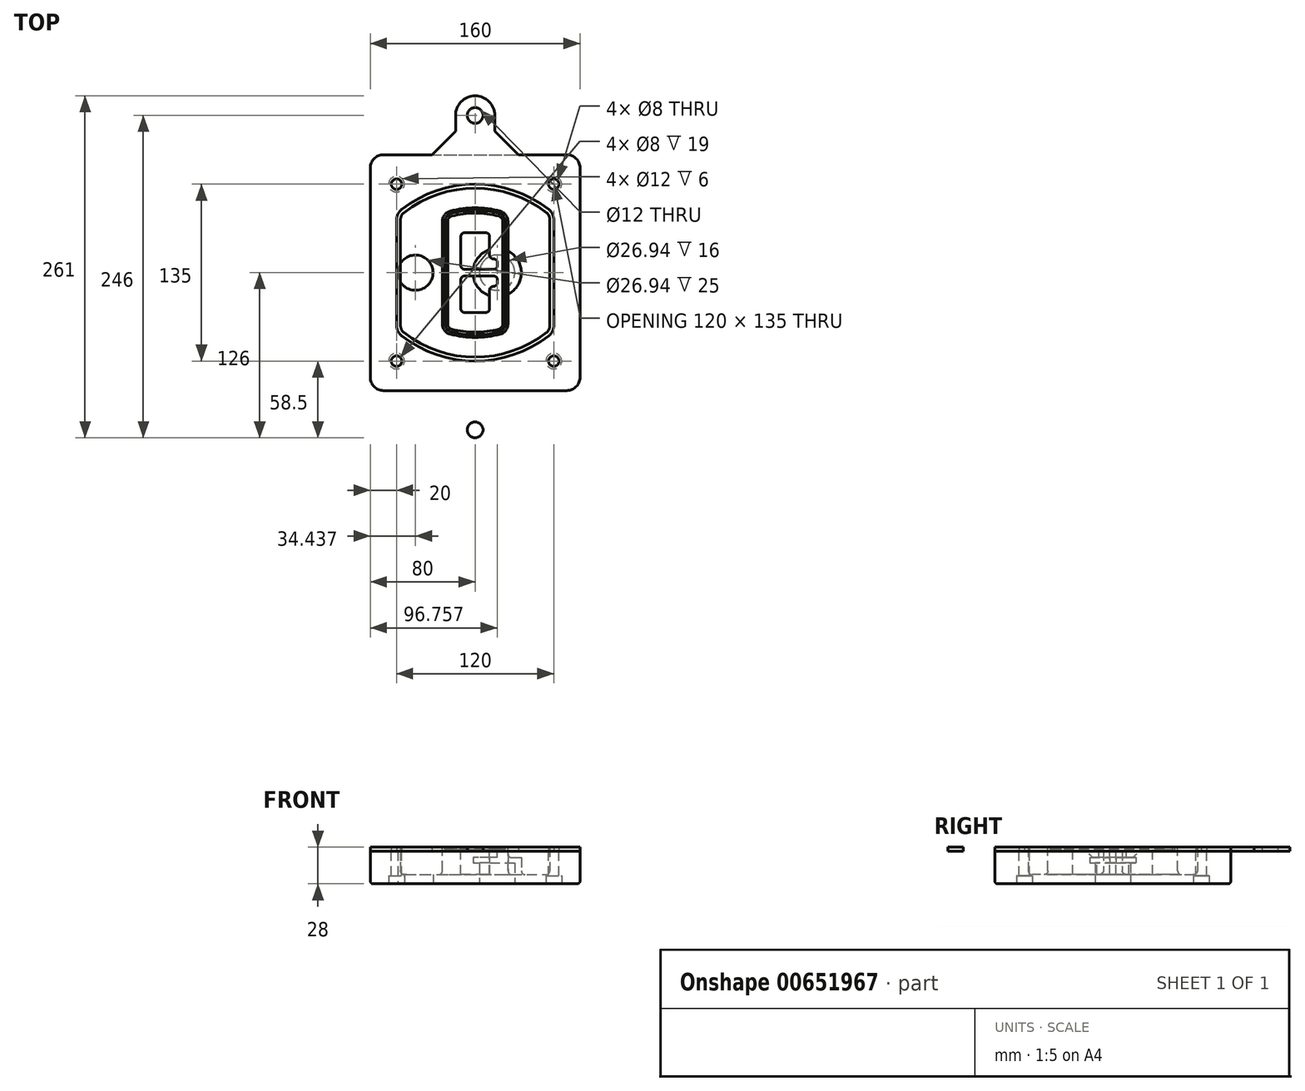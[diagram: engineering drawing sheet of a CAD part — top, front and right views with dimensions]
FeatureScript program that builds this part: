
annotation { "Feature Type Name" : "Feature", "Feature Type Description" : "" }
export const myFeature = defineFeature(function(context is Context, id is Id, definition is map)
    precondition{}
    {
        {
            var Q0;
            Q0=qCreatedBy(makeId("Top.planeOp"),FACE);
            var sketch = newSketch(context, id + "F0", { "sketchPlane" : qUnion([Q0])});
            skPoint(sketch, "E0.rect.middle", {"position": v(0, 0) * mm});
            skLineSegment(sketch, "E1.bottom", {"start": v(-70, -90) * mm, "end": v(70, -90) * mm});
            skLineSegment(sketch, "E1.top", {"start": v(-70, 90) * mm, "end": v(70, 90) * mm});
            skLineSegment(sketch, "E1.left", {"start": v(-80, -80) * mm, "end": v(-80, 80) * mm});
            skLineSegment(sketch, "E1.right", {"start": v(80, -80) * mm, "end": v(80, 80) * mm});
            skLineSegment(sketch, "E2", {"start": v(-80, 90) * mm, "end": v(80, -90) * mm, "construction": true});
            skLineSegment(sketch, "E3", {"start": v(80, 90) * mm, "end": v(-80, -90) * mm, "construction": true});
            skCircle(sketch, "E4", {"center": v(-60, 67.5) * mm, "radius": 4 * mm});
            skCircle(sketch, "E5", {"center": v(60, 67.5) * mm, "radius": 4 * mm});
            skCircle(sketch, "E6", {"center": v(60, -67.5) * mm, "radius": 4 * mm});
            skCircle(sketch, "E7", {"center": v(-60, -67.5) * mm, "radius": 4 * mm});
            skLineSegment(sketch, "E8", {"start": v(-60, 67.5) * mm, "end": v(60, 67.5) * mm, "construction": true});
            skLineSegment(sketch, "E9", {"start": v(60, 67.5) * mm, "end": v(60, -67.5) * mm, "construction": true});
            skLineSegment(sketch, "E10", {"start": v(60, -67.5) * mm, "end": v(-60, -67.5) * mm, "construction": true});
            skLineSegment(sketch, "E11", {"start": v(-60, -67.5) * mm, "end": v(-60, 67.5) * mm, "construction": true});
            skLineSegment(sketch, "E12", {"start": v(-60, 40.3) * mm, "end": v(-60, -40.3) * mm});
            skLineSegment(sketch, "E13", {"start": v(60, 40.3) * mm, "end": v(60, -40.3) * mm});
            skArc(sketch, "E14", {"start": v(56.15, 48.18) * mm, "mid": v(0, 67.5) * mm, "end": v(-56.15, 48.18) * mm});
            skArc(sketch, "E15", {"start": v(-56.15, -48.18) * mm, "mid": v(0, -67.5) * mm, "end": v(56.15, -48.18) * mm});
            skLineSegment(sketch, "E16", {"start": v(-60, 0) * mm, "end": v(60, 0) * mm, "construction": true});
            skPoint(sketch, "E17.visualSharp", {"position": v(-60, -45) * mm});
            skArc(sketch, "E17.filletArc", {"start": v(-60, -40.3) * mm, "mid": v(-58.99, -44.68) * mm, "end": v(-56.15, -48.18) * mm});
            skPoint(sketch, "E18.visualSharp", {"position": v(-60, 45) * mm});
            skArc(sketch, "E18.filletArc", {"start": v(-56.15, 48.18) * mm, "mid": v(-58.99, 44.68) * mm, "end": v(-60, 40.3) * mm});
            skPoint(sketch, "E19.visualSharp", {"position": v(60, 45) * mm});
            skArc(sketch, "E19.filletArc", {"start": v(60, 40.3) * mm, "mid": v(58.99, 44.68) * mm, "end": v(56.15, 48.18) * mm});
            skPoint(sketch, "E20.visualSharp", {"position": v(60, -45) * mm});
            skArc(sketch, "E20.filletArc", {"start": v(56.15, -48.18) * mm, "mid": v(58.99, -44.68) * mm, "end": v(60, -40.3) * mm});
            skPoint(sketch, "E21.visualSharp", {"position": v(-80, 90) * mm});
            skArc(sketch, "E21.filletArc", {"start": v(-70, 90) * mm, "mid": v(-77.07, 87.07) * mm, "end": v(-80, 80) * mm});
            skPoint(sketch, "E22.visualSharp", {"position": v(80, 90) * mm});
            skArc(sketch, "E22.filletArc", {"start": v(80, 80) * mm, "mid": v(77.07, 87.07) * mm, "end": v(70, 90) * mm});
            skPoint(sketch, "E23.visualSharp", {"position": v(80, -90) * mm});
            skArc(sketch, "E23.filletArc", {"start": v(70, -90) * mm, "mid": v(77.07, -87.07) * mm, "end": v(80, -80) * mm});
            skPoint(sketch, "E24.visualSharp", {"position": v(-80, -90) * mm});
            skArc(sketch, "E24.filletArc", {"start": v(-80, -80) * mm, "mid": v(-77.07, -87.07) * mm, "end": v(-70, -90) * mm});
            skArc(sketch, "E25.0", {"start": v(57, 40.3) * mm, "mid": v(56.3, 43.36) * mm, "end": v(54.3, 45.81) * mm});
            skLineSegment(sketch, "E25.1", {"start": v(57, 40.3) * mm, "end": v(57, -40.3) * mm});
            skArc(sketch, "E25.2", {"start": v(54.3, -45.81) * mm, "mid": v(56.3, -43.36) * mm, "end": v(57, -40.3) * mm});
            skArc(sketch, "E25.3", {"start": v(-54.3, -45.81) * mm, "mid": v(0, -64.5) * mm, "end": v(54.3, -45.81) * mm});
            skArc(sketch, "E25.4", {"start": v(-57, -40.3) * mm, "mid": v(-56.3, -43.36) * mm, "end": v(-54.3, -45.81) * mm});
            skArc(sketch, "E25.5", {"start": v(54.3, 45.81) * mm, "mid": v(0, 64.5) * mm, "end": v(-54.3, 45.81) * mm});
            skLineSegment(sketch, "E25.6", {"start": v(-57, 40.3) * mm, "end": v(-57, -40.3) * mm});
            skArc(sketch, "E25.7", {"start": v(-54.3, 45.81) * mm, "mid": v(-56.3, 43.36) * mm, "end": v(-57, 40.3) * mm});
            skArc(sketch, "E26.0", {"start": v(-58.62, 51.33) * mm, "mid": v(-62.58, 46.43) * mm, "end": v(-64, 40.3) * mm});
            skArc(sketch, "E26.1", {"start": v(58.62, 51.33) * mm, "mid": v(0, 71.5) * mm, "end": v(-58.62, 51.33) * mm});
            skArc(sketch, "E26.2", {"start": v(64, 40.3) * mm, "mid": v(62.58, 46.43) * mm, "end": v(58.62, 51.33) * mm});
            skLineSegment(sketch, "E26.3", {"start": v(64, 40.3) * mm, "end": v(64, -40.3) * mm});
            skArc(sketch, "E26.4", {"start": v(58.62, -51.33) * mm, "mid": v(62.58, -46.43) * mm, "end": v(64, -40.3) * mm});
            skLineSegment(sketch, "E26.5", {"start": v(-64, 40.3) * mm, "end": v(-64, -40.3) * mm});
            skArc(sketch, "E26.6", {"start": v(-58.62, -51.33) * mm, "mid": v(0, -71.5) * mm, "end": v(58.62, -51.33) * mm});
            skArc(sketch, "E26.7", {"start": v(-64, -40.3) * mm, "mid": v(-62.58, -46.43) * mm, "end": v(-58.62, -51.33) * mm});
            skSolve(sketch);
        }
        {
            var Q0;
            Q0=makeQuery(id+"F0.imprint","IMPRINT",FACE,{"disambiguationData":[TD([[makeQuery(id+"F0.imprint","IMPRINT",EDGE,{"derivedFrom":sQuery(id+"F0.wireOp",EDGE,"E1.bottom")}),1.0]])]});
            var Q1;
            Q1=makeQuery(id+"F0.imprint","IMPRINT",FACE,{"disambiguationData":[TD([[makeQuery(id+"F0.imprint","IMPRINT",EDGE,{"derivedFrom":sQuery(id+"F0.wireOp",EDGE,"E12")}),1.0]])]});
            var Q2;
            Q2=makeQuery(id+"F0.imprint","IMPRINT",FACE,{"disambiguationData":[TD([[makeQuery(id+"F0.imprint","IMPRINT",EDGE,{"derivedFrom":sQuery(id+"F0.wireOp",EDGE,"E25.0")}),1.0]])]});
            var Q3;
            Q3=makeQuery(id+"F0.imprint","IMPRINT",FACE,{"disambiguationData":[TD([[makeQuery(id+"F0.imprint","IMPRINT",EDGE,{"derivedFrom":sQuery(id+"F0.wireOp",EDGE,"E12")}),-1.0]])]});
            extrude(context, id + "F1", {"entities" : qUnion([Q0, Q1, Q2, Q3]), "oppositeDirection" : true, "depth" : 25 * mm});
        }
        {
            var Q0;
            Q0=makeQuery(id+"F0.imprint","IMPRINT",FACE,{"disambiguationData":[TD([[makeQuery(id+"F0.imprint","IMPRINT",EDGE,{"derivedFrom":sQuery(id+"F0.wireOp",EDGE,"E12")}),1.0]])]});
            extrude(context, id + "F2", {"entities" : qUnion([Q0]), "operationType" : NewBodyOperationType.ADD, "depth" : 3 * mm});
        }
        {
            var Q0;
            Q0=makeQuery(id+"F0.imprint","IMPRINT",FACE,{"disambiguationData":[TD([[makeQuery(id+"F0.imprint","IMPRINT",EDGE,{"derivedFrom":sQuery(id+"F0.wireOp",EDGE,"E25.0")}),1.0]])]});
            extrude(context, id + "F3", {"entities" : qUnion([Q0]), "operationType" : NewBodyOperationType.REMOVE, "oppositeDirection" : true, "depth" : 18 * mm});
        }
        {
            var Q0;
            Q0=makeQuery(id+"F2.opExtrude","CAP_FACE",FACE,{"disambiguationData":[OSD([sQuery(id+"F0.wireOp",EDGE,"E12"),sQuery(id+"F0.wireOp",EDGE,"E13"),sQuery(id+"F0.wireOp",EDGE,"E14"),sQuery(id+"F0.wireOp",EDGE,"E15"),sQuery(id+"F0.wireOp",EDGE,"E17.filletArc"),sQuery(id+"F0.wireOp",EDGE,"E18.filletArc"),sQuery(id+"F0.wireOp",EDGE,"E19.filletArc"),sQuery(id+"F0.wireOp",EDGE,"E20.filletArc"),sQuery(id+"F0.wireOp",EDGE,"E25.0"),sQuery(id+"F0.wireOp",EDGE,"E25.1"),sQuery(id+"F0.wireOp",EDGE,"E25.2"),sQuery(id+"F0.wireOp",EDGE,"E25.3"),sQuery(id+"F0.wireOp",EDGE,"E25.4"),sQuery(id+"F0.wireOp",EDGE,"E25.5"),sQuery(id+"F0.wireOp",EDGE,"E25.6"),sQuery(id+"F0.wireOp",EDGE,"E25.7")])],"isStart":false});
            var sketch = newSketch(context, id + "F4", { "sketchPlane" : qUnion([Q0])});
            skArc(sketch, "E27.0", {"start": v(-19.08, -46.97) * mm, "mid": v(0, -49.5) * mm, "end": v(19.08, -46.97) * mm});
            skArc(sketch, "E28.0", {"start": v(19.08, 46.97) * mm, "mid": v(0, 49.5) * mm, "end": v(-19.08, 46.97) * mm});
            skLineSegment(sketch, "E29", {"start": v(-25, 39.25) * mm, "end": v(-25, -39.25) * mm});
            skLineSegment(sketch, "E30", {"start": v(25, 39.25) * mm, "end": v(25, -39.25) * mm});
            skLineSegment(sketch, "E31", {"start": v(-25, 45.1) * mm, "end": v(25, 45.1) * mm, "construction": true});
            skLineSegment(sketch, "E32", {"start": v(-25, -45.1) * mm, "end": v(25, -45.1) * mm, "construction": true});
            skPoint(sketch, "E33.visualSharp", {"position": v(-25, 45.1) * mm});
            skArc(sketch, "E33.filletArc", {"start": v(-19.08, 46.97) * mm, "mid": v(-23.35, 44.11) * mm, "end": v(-25, 39.25) * mm});
            skPoint(sketch, "E34.visualSharp", {"position": v(25, 45.1) * mm});
            skArc(sketch, "E34.filletArc", {"start": v(25, 39.25) * mm, "mid": v(23.35, 44.11) * mm, "end": v(19.08, 46.97) * mm});
            skPoint(sketch, "E35.visualSharp", {"position": v(25, -45.1) * mm});
            skArc(sketch, "E35.filletArc", {"start": v(19.08, -46.97) * mm, "mid": v(23.35, -44.11) * mm, "end": v(25, -39.25) * mm});
            skPoint(sketch, "E36.visualSharp", {"position": v(-25, -45.1) * mm});
            skArc(sketch, "E36.filletArc", {"start": v(-25, -39.25) * mm, "mid": v(-23.35, -44.11) * mm, "end": v(-19.08, -46.97) * mm});
            skArc(sketch, "E37.0", {"start": v(54.3, 45.81) * mm, "mid": v(0, 64.5) * mm, "end": v(-54.3, 45.81) * mm});
            skArc(sketch, "E37.1", {"start": v(-54.3, 45.81) * mm, "mid": v(-56.3, 43.36) * mm, "end": v(-57, 40.3) * mm});
            skLineSegment(sketch, "E37.2", {"start": v(-57, 40.3) * mm, "end": v(-57, -40.3) * mm});
            skArc(sketch, "E37.3", {"start": v(-57, -40.3) * mm, "mid": v(-56.3, -43.36) * mm, "end": v(-54.3, -45.81) * mm});
            skArc(sketch, "E37.4", {"start": v(-54.3, -45.81) * mm, "mid": v(0, -64.5) * mm, "end": v(54.3, -45.81) * mm});
            skArc(sketch, "E37.5", {"start": v(54.3, -45.81) * mm, "mid": v(56.3, -43.36) * mm, "end": v(57, -40.3) * mm});
            skLineSegment(sketch, "E37.6", {"start": v(57, 40.3) * mm, "end": v(57, -40.3) * mm});
            skArc(sketch, "E37.7", {"start": v(57, 40.3) * mm, "mid": v(56.3, 43.36) * mm, "end": v(54.3, 45.81) * mm});
            skLineSegment(sketch, "E38.0", {"start": v(23, 39.25) * mm, "end": v(23, -39.25) * mm});
            skArc(sketch, "E38.1", {"start": v(18.56, -45.04) * mm, "mid": v(21.76, -42.9) * mm, "end": v(23, -39.25) * mm});
            skArc(sketch, "E38.2", {"start": v(-18.56, -45.04) * mm, "mid": v(0, -47.5) * mm, "end": v(18.56, -45.04) * mm});
            skArc(sketch, "E38.3", {"start": v(-23, -39.25) * mm, "mid": v(-21.76, -42.9) * mm, "end": v(-18.56, -45.04) * mm});
            skLineSegment(sketch, "E38.4", {"start": v(-23, 39.25) * mm, "end": v(-23, -39.25) * mm});
            skArc(sketch, "E38.5", {"start": v(23, 39.25) * mm, "mid": v(21.76, 42.9) * mm, "end": v(18.56, 45.04) * mm});
            skArc(sketch, "E38.6", {"start": v(-18.56, 45.04) * mm, "mid": v(-21.76, 42.9) * mm, "end": v(-23, 39.25) * mm});
            skArc(sketch, "E38.7", {"start": v(18.56, 45.04) * mm, "mid": v(0, 47.5) * mm, "end": v(-18.56, 45.04) * mm});
            skArc(sketch, "E39.0", {"start": v(21, 39.25) * mm, "mid": v(20.18, 41.68) * mm, "end": v(18.04, 43.1) * mm});
            skLineSegment(sketch, "E39.1", {"start": v(21, 39.25) * mm, "end": v(21, -39.25) * mm});
            skArc(sketch, "E39.2", {"start": v(18.04, -43.1) * mm, "mid": v(20.18, -41.68) * mm, "end": v(21, -39.25) * mm});
            skArc(sketch, "E39.3", {"start": v(-18.04, -43.1) * mm, "mid": v(0, -45.5) * mm, "end": v(18.04, -43.1) * mm});
            skArc(sketch, "E39.4", {"start": v(-21, -39.25) * mm, "mid": v(-20.18, -41.68) * mm, "end": v(-18.04, -43.1) * mm});
            skArc(sketch, "E39.5", {"start": v(18.04, 43.1) * mm, "mid": v(0, 45.5) * mm, "end": v(-18.04, 43.1) * mm});
            skLineSegment(sketch, "E39.6", {"start": v(-21, 39.25) * mm, "end": v(-21, -39.25) * mm});
            skArc(sketch, "E39.7", {"start": v(-18.04, 43.1) * mm, "mid": v(-20.18, 41.68) * mm, "end": v(-21, 39.25) * mm});
            skLineSegment(sketch, "E40", {"start": v(-25, 0) * mm, "end": v(25, 0) * mm, "construction": true});
            skLineSegment(sketch, "E41", {"start": v(-11, 5.5) * mm, "end": v(-11, 27.5) * mm});
            skLineSegment(sketch, "E42", {"start": v(-8, 30.5) * mm, "end": v(8, 30.5) * mm});
            skLineSegment(sketch, "E43", {"start": v(11, 27.5) * mm, "end": v(11, 13.5) * mm});
            skLineSegment(sketch, "E44", {"start": v(14, 10.5) * mm, "end": v(14, 10.5) * mm});
            skLineSegment(sketch, "E45", {"start": v(17, 7.5) * mm, "end": v(17, 5.5) * mm});
            skLineSegment(sketch, "E46", {"start": v(14, 2.5) * mm, "end": v(-8, 2.5) * mm});
            skPoint(sketch, "E47.visualSharp", {"position": v(-11, 30.5) * mm});
            skArc(sketch, "E47.filletArc", {"start": v(-8, 30.5) * mm, "mid": v(-10.12, 29.62) * mm, "end": v(-11, 27.5) * mm});
            skPoint(sketch, "E48.visualSharp", {"position": v(11, 30.5) * mm});
            skArc(sketch, "E48.filletArc", {"start": v(11, 27.5) * mm, "mid": v(10.12, 29.62) * mm, "end": v(8, 30.5) * mm});
            skPoint(sketch, "E49.visualSharp", {"position": v(11, 10.5) * mm});
            skArc(sketch, "E49.filletArc", {"start": v(11, 13.5) * mm, "mid": v(11.88, 11.38) * mm, "end": v(14, 10.5) * mm});
            skPoint(sketch, "E50.visualSharp", {"position": v(17, 10.5) * mm});
            skArc(sketch, "E50.filletArc", {"start": v(17, 7.5) * mm, "mid": v(16.12, 9.62) * mm, "end": v(14, 10.5) * mm});
            skPoint(sketch, "E51.visualSharp", {"position": v(17, 2.5) * mm});
            skArc(sketch, "E51.filletArc", {"start": v(14, 2.5) * mm, "mid": v(16.12, 3.38) * mm, "end": v(17, 5.5) * mm});
            skPoint(sketch, "E52.visualSharp", {"position": v(-11, 2.5) * mm});
            skArc(sketch, "E52.filletArc", {"start": v(-11, 5.5) * mm, "mid": v(-10.12, 3.38) * mm, "end": v(-8, 2.5) * mm});
            skLineSegment(sketch, "E53.0.MirrorCS", {"start": v(14, -2.5) * mm, "end": v(-8, -2.5) * mm});
            skArc(sketch, "E54.0.MirrorCS", {"start": v(-11, -5.5) * mm, "mid": v(-10.12, -3.38) * mm, "end": v(-8, -2.5) * mm});
            skLineSegment(sketch, "E55.0.MirrorCS", {"start": v(-11, -5.5) * mm, "end": v(-11, -27.5) * mm});
            skArc(sketch, "E56.0.MirrorCS", {"start": v(-8, -30.5) * mm, "mid": v(-10.12, -29.62) * mm, "end": v(-11, -27.5) * mm});
            skLineSegment(sketch, "E57.0.MirrorCS", {"start": v(-8, -30.5) * mm, "end": v(8, -30.5) * mm});
            skArc(sketch, "E58.0.MirrorCS", {"start": v(11, -27.5) * mm, "mid": v(10.12, -29.62) * mm, "end": v(8, -30.5) * mm});
            skLineSegment(sketch, "E59.0.MirrorCS", {"start": v(11, -27.5) * mm, "end": v(11, -13.5) * mm});
            skArc(sketch, "E60.0.MirrorCS", {"start": v(11, -13.5) * mm, "mid": v(11.88, -11.38) * mm, "end": v(14, -10.5) * mm});
            skArc(sketch, "E61.0.MirrorCS", {"start": v(17, -7.5) * mm, "mid": v(16.12, -9.62) * mm, "end": v(14, -10.5) * mm});
            skLineSegment(sketch, "E62.0.MirrorCS", {"start": v(17, -7.5) * mm, "end": v(17, -5.5) * mm});
            skArc(sketch, "E63.0.MirrorCS", {"start": v(14, -2.5) * mm, "mid": v(16.12, -3.38) * mm, "end": v(17, -5.5) * mm});
            skSolve(sketch);
        }
        {
            var Q0;
            Q0=makeQuery(id+"F4.imprint","IMPRINT",FACE,{"disambiguationData":[TD([[makeQuery(id+"F4.imprint","IMPRINT",EDGE,{"derivedFrom":sQuery(id+"F4.wireOp",EDGE,"E27.0")}),1.0]])]});
            var Q1;
            Q1=makeQuery(id+"F4.imprint","IMPRINT",FACE,{"disambiguationData":[TD([[makeQuery(id+"F4.imprint","IMPRINT",EDGE,{"derivedFrom":sQuery(id+"F4.wireOp",EDGE,"E38.0")}),-1.0]])]});
            var Q2;
            Q2=makeQuery(id+"F4.imprint","IMPRINT",FACE,{"disambiguationData":[TD([[makeQuery(id+"F4.imprint","IMPRINT",EDGE,{"derivedFrom":sQuery(id+"F4.wireOp",EDGE,"E39.0")}),1.0]])]});
            extrude(context, id + "F5", {"entities" : qUnion([Q0, Q1, Q2]), "operationType" : NewBodyOperationType.ADD, "endBound" : BoundingType.UP_TO_NEXT, "oppositeDirection" : true, "depth" : 25 * mm});
        }
        {
            var Q0;
            Q0=makeQuery(id+"F4.imprint","IMPRINT",FACE,{"disambiguationData":[TD([[makeQuery(id+"F4.imprint","IMPRINT",EDGE,{"derivedFrom":sQuery(id+"F4.wireOp",EDGE,"E38.0")}),-1.0]])]});
            extrude(context, id + "F6", {"entities" : qUnion([Q0]), "operationType" : NewBodyOperationType.REMOVE, "oppositeDirection" : true, "depth" : 2 * mm});
        }
        {
            var Q0;
            Q0=makeQuery(id+"F1.opExtrude","CAP_FACE",FACE,{"disambiguationData":[OSD([sQuery(id+"F0.wireOp",EDGE,"E1.bottom"),sQuery(id+"F0.wireOp",EDGE,"E1.top"),sQuery(id+"F0.wireOp",EDGE,"E1.left"),sQuery(id+"F0.wireOp",EDGE,"E1.right"),sQuery(id+"F0.wireOp",EDGE,"E4"),sQuery(id+"F0.wireOp",EDGE,"E5"),sQuery(id+"F0.wireOp",EDGE,"E6"),sQuery(id+"F0.wireOp",EDGE,"E7"),sQuery(id+"F0.wireOp",EDGE,"E21.filletArc"),sQuery(id+"F0.wireOp",EDGE,"E22.filletArc"),sQuery(id+"F0.wireOp",EDGE,"E23.filletArc"),sQuery(id+"F0.wireOp",EDGE,"E24.filletArc")])],"isStart":false});
            var sketch = newSketch(context, id + "F7", { "sketchPlane" : qUnion([Q0])});
            skCircle(sketch, "E64", {"center": v(16.76, 0) * mm, "radius": 13.47 * mm});
            skCircle(sketch, "E65", {"center": v(-45.56, 0) * mm, "radius": 13.47 * mm});
            skLineSegment(sketch, "E66", {"start": v(80, 0) * mm, "end": v(-80, 0) * mm});
            skCircle(sketch, "E67", {"center": v(16.76, 0) * mm, "radius": 18.47 * mm});
            skCircle(sketch, "E68", {"center": v(60, -67.5) * mm, "radius": 6 * mm});
            skCircle(sketch, "E69", {"center": v(-60, -67.5) * mm, "radius": 6 * mm});
            skCircle(sketch, "E70", {"center": v(-60, 67.5) * mm, "radius": 6 * mm});
            skCircle(sketch, "E71", {"center": v(60, 67.5) * mm, "radius": 6 * mm});
            skSolve(sketch);
        }
        {
            var Q0;
            {var subQ1=sQuery(id+"F7.wireOp",EDGE,"E66");var subQ4=sQuery(id+"F7.wireOp",EDGE,"E64");var subQ6=makeQuery(id+"F7.imprint","INTERSECT",VERTEX,{"disambiguationData":[OD(0.0)],"derivedFrom":[subQ4,subQ1]});Q0=makeQuery(id+"F7.imprint","IMPRINT",FACE,{"disambiguationData":[TD([[makeQuery(id+"F7.imprint","IMPRINT",EDGE,{"disambiguationData":[TD([[subQ6,-1.0]])],"derivedFrom":subQ4}),-1.0]])]});}
            var Q1;
            {var subQ0=sQuery(id+"F7.wireOp",EDGE,"E66");var subQ1=sQuery(id+"F7.wireOp",EDGE,"E64");var subQ3=makeQuery(id+"F7.imprint","INTERSECT",VERTEX,{"disambiguationData":[OD(0.0)],"derivedFrom":[subQ1,subQ0]});Q1=makeQuery(id+"F7.imprint","IMPRINT",FACE,{"disambiguationData":[TD([[makeQuery(id+"F7.imprint","IMPRINT",EDGE,{"disambiguationData":[TD([[subQ3,-1.0]])],"derivedFrom":subQ1}),1.0]])]});}
            var Q2;
            {var subQ0=sQuery(id+"F7.wireOp",EDGE,"E66");var subQ1=sQuery(id+"F7.wireOp",EDGE,"E64");var subQ3=makeQuery(id+"F7.imprint","INTERSECT",VERTEX,{"disambiguationData":[OD(0.0)],"derivedFrom":[subQ1,subQ0]});Q2=makeQuery(id+"F7.imprint","IMPRINT",FACE,{"disambiguationData":[TD([[makeQuery(id+"F7.imprint","IMPRINT",EDGE,{"disambiguationData":[TD([[subQ3,1.0]])],"derivedFrom":subQ1}),1.0]])]});}
            var Q3;
            {var subQ1=sQuery(id+"F7.wireOp",EDGE,"E66");var subQ4=sQuery(id+"F7.wireOp",EDGE,"E64");var subQ6=makeQuery(id+"F7.imprint","INTERSECT",VERTEX,{"disambiguationData":[OD(0.0)],"derivedFrom":[subQ4,subQ1]});Q3=makeQuery(id+"F7.imprint","IMPRINT",FACE,{"disambiguationData":[TD([[makeQuery(id+"F7.imprint","IMPRINT",EDGE,{"disambiguationData":[TD([[subQ6,1.0]])],"derivedFrom":subQ4}),-1.0]])]});}
            extrude(context, id + "F8", {"entities" : qUnion([Q0, Q1, Q2, Q3]), "operationType" : NewBodyOperationType.ADD, "oppositeDirection" : true, "depth" : 20 * mm});
        }
        {
            var Q0;
            {var subQ0=sQuery(id+"F7.wireOp",EDGE,"E66");var subQ1=sQuery(id+"F7.wireOp",EDGE,"E64");var subQ3=makeQuery(id+"F7.imprint","INTERSECT",VERTEX,{"disambiguationData":[OD(0.0)],"derivedFrom":[subQ1,subQ0]});Q0=makeQuery(id+"F7.imprint","IMPRINT",FACE,{"disambiguationData":[TD([[makeQuery(id+"F7.imprint","IMPRINT",EDGE,{"disambiguationData":[TD([[subQ3,-1.0]])],"derivedFrom":subQ1}),1.0]])]});}
            var Q1;
            {var subQ0=sQuery(id+"F7.wireOp",EDGE,"E66");var subQ1=sQuery(id+"F7.wireOp",EDGE,"E64");var subQ3=makeQuery(id+"F7.imprint","INTERSECT",VERTEX,{"disambiguationData":[OD(0.0)],"derivedFrom":[subQ1,subQ0]});Q1=makeQuery(id+"F7.imprint","IMPRINT",FACE,{"disambiguationData":[TD([[makeQuery(id+"F7.imprint","IMPRINT",EDGE,{"disambiguationData":[TD([[subQ3,1.0]])],"derivedFrom":subQ1}),1.0]])]});}
            extrude(context, id + "F9", {"entities" : qUnion([Q0, Q1]), "operationType" : NewBodyOperationType.REMOVE, "oppositeDirection" : true, "depth" : 16 * mm});
        }
        {
            var Q0;
            {var subQ0=sQuery(id+"F7.wireOp",EDGE,"E66");var subQ1=sQuery(id+"F7.wireOp",EDGE,"E65");var subQ3=makeQuery(id+"F7.imprint","INTERSECT",VERTEX,{"disambiguationData":[OD(0.0)],"derivedFrom":[subQ1,subQ0]});Q0=makeQuery(id+"F7.imprint","IMPRINT",FACE,{"disambiguationData":[TD([[makeQuery(id+"F7.imprint","IMPRINT",EDGE,{"disambiguationData":[TD([[subQ3,-1.0]])],"derivedFrom":subQ1}),1.0]])]});}
            var Q1;
            {var subQ0=sQuery(id+"F7.wireOp",EDGE,"E66");var subQ1=sQuery(id+"F7.wireOp",EDGE,"E65");var subQ3=makeQuery(id+"F7.imprint","INTERSECT",VERTEX,{"disambiguationData":[OD(0.0)],"derivedFrom":[subQ1,subQ0]});Q1=makeQuery(id+"F7.imprint","IMPRINT",FACE,{"disambiguationData":[TD([[makeQuery(id+"F7.imprint","IMPRINT",EDGE,{"disambiguationData":[TD([[subQ3,1.0]])],"derivedFrom":subQ1}),1.0]])]});}
            extrude(context, id + "F10", {"entities" : qUnion([Q0, Q1]), "operationType" : NewBodyOperationType.REMOVE, "oppositeDirection" : true, "depth" : 25 * mm});
        }
        {
            var Q0;
            Q0=makeQuery(id+"F7.imprint","IMPRINT",FACE,{"disambiguationData":[TD([[makeQuery(id+"F7.imprint","IMPRINT",EDGE,{"derivedFrom":sQuery(id+"F7.wireOp",EDGE,"E68")}),1.0]])]});
            var Q1;
            Q1=makeQuery(id+"F7.imprint","IMPRINT",FACE,{"disambiguationData":[TD([[makeQuery(id+"F7.imprint","IMPRINT",EDGE,{"derivedFrom":makeQuery(id+"F1.opExtrude","CAP_EDGE",EDGE,{"disambiguationData":[OSD([sQuery(id+"F0.wireOp",EDGE,"E5")])],"isStart":false})}),-1.0]])]});
            var Q2;
            Q2=makeQuery(id+"F7.imprint","IMPRINT",FACE,{"disambiguationData":[TD([[makeQuery(id+"F7.imprint","IMPRINT",EDGE,{"derivedFrom":sQuery(id+"F7.wireOp",EDGE,"E69")}),1.0]])]});
            var Q3;
            Q3=makeQuery(id+"F7.imprint","IMPRINT",FACE,{"disambiguationData":[TD([[makeQuery(id+"F7.imprint","IMPRINT",EDGE,{"derivedFrom":makeQuery(id+"F1.opExtrude","CAP_EDGE",EDGE,{"disambiguationData":[OSD([sQuery(id+"F0.wireOp",EDGE,"E4")])],"isStart":false})}),-1.0]])]});
            var Q4;
            Q4=makeQuery(id+"F7.imprint","IMPRINT",FACE,{"disambiguationData":[TD([[makeQuery(id+"F7.imprint","IMPRINT",EDGE,{"derivedFrom":sQuery(id+"F7.wireOp",EDGE,"E70")}),1.0]])]});
            var Q5;
            Q5=makeQuery(id+"F7.imprint","IMPRINT",FACE,{"disambiguationData":[TD([[makeQuery(id+"F7.imprint","IMPRINT",EDGE,{"derivedFrom":makeQuery(id+"F1.opExtrude","CAP_EDGE",EDGE,{"disambiguationData":[OSD([sQuery(id+"F0.wireOp",EDGE,"E7")])],"isStart":false})}),-1.0]])]});
            var Q6;
            Q6=makeQuery(id+"F7.imprint","IMPRINT",FACE,{"disambiguationData":[TD([[makeQuery(id+"F7.imprint","IMPRINT",EDGE,{"derivedFrom":sQuery(id+"F7.wireOp",EDGE,"E71")}),1.0]])]});
            var Q7;
            Q7=makeQuery(id+"F7.imprint","IMPRINT",FACE,{"disambiguationData":[TD([[makeQuery(id+"F7.imprint","IMPRINT",EDGE,{"derivedFrom":makeQuery(id+"F1.opExtrude","CAP_EDGE",EDGE,{"disambiguationData":[OSD([sQuery(id+"F0.wireOp",EDGE,"E6")])],"isStart":false})}),-1.0]])]});
            extrude(context, id + "F11", {"entities" : qUnion([Q0, Q1, Q2, Q3, Q4, Q5, Q6, Q7]), "operationType" : NewBodyOperationType.REMOVE, "oppositeDirection" : true, "depth" : 6 * mm});
        }
        {
            var Q0;
            Q0=makeQuery(id+"F9.boolean.opBoolean","COPY",FACE,{"derivedFrom":makeQuery(id+"F9.opExtrude","CAP_FACE",FACE,{"disambiguationData":[OSD([sQuery(id+"F7.wireOp",EDGE,"E64")])],"isStart":false})});
            var sketch = newSketch(context, id + "F12", { "sketchPlane" : qUnion([Q0])});
            skArc(sketch, "E72.0", {"start": v(11, 17.55) * mm, "mid": v(2.57, 11.82) * mm, "end": v(-1.54, 2.5) * mm});
            skArc(sketch, "E72.1", {"start": v(-1.54, -2.5) * mm, "mid": v(2.57, -11.82) * mm, "end": v(11, -17.55) * mm});
            skLineSegment(sketch, "E73", {"start": v(-1.54, -2.5) * mm, "end": v(14, -2.5) * mm});
            skLineSegment(sketch, "E74.0", {"start": v(14, 2.5) * mm, "end": v(-1.54, 2.5) * mm});
            skArc(sketch, "E74.1", {"start": v(14, 2.5) * mm, "mid": v(16.12, 3.38) * mm, "end": v(17, 5.5) * mm});
            skLineSegment(sketch, "E74.2", {"start": v(17, 7.5) * mm, "end": v(17, 5.5) * mm});
            skArc(sketch, "E74.3", {"start": v(17, 7.5) * mm, "mid": v(16.12, 9.62) * mm, "end": v(14, 10.5) * mm});
            skArc(sketch, "E74.4", {"start": v(11, 13.5) * mm, "mid": v(11.88, 11.38) * mm, "end": v(14, 10.5) * mm});
            skLineSegment(sketch, "E74.5", {"start": v(11, 17.55) * mm, "end": v(11, 13.5) * mm});
            skLineSegment(sketch, "E74.7", {"start": v(14, -2.5) * mm, "end": v(-1.54, -2.5) * mm});
            skArc(sketch, "E74.8", {"start": v(14, -2.5) * mm, "mid": v(16.12, -3.38) * mm, "end": v(17, -5.5) * mm});
            skLineSegment(sketch, "E74.9", {"start": v(17, -7.5) * mm, "end": v(17, -5.5) * mm});
            skArc(sketch, "E74.10", {"start": v(17, -7.5) * mm, "mid": v(16.12, -9.62) * mm, "end": v(14, -10.5) * mm});
            skArc(sketch, "E74.11", {"start": v(11, -13.5) * mm, "mid": v(11.88, -11.38) * mm, "end": v(14, -10.5) * mm});
            skLineSegment(sketch, "E74.12", {"start": v(11, -17.55) * mm, "end": v(11, -13.5) * mm});
            skPoint(sketch, "E75.orphan", {"position": v(11, -27.5) * mm});
            skPoint(sketch, "E76.orphan", {"position": v(-8, -2.5) * mm});
            skPoint(sketch, "E77.orphan", {"position": v(-8, 2.5) * mm});
            skPoint(sketch, "E78.orphan", {"position": v(11, 27.5) * mm});
            skSolve(sketch);
        }
        {
            var Q0;
            {var subQ7=sQuery(id+"F12.wireOp",EDGE,"E72.0");var subQ14=sQuery(id+"F12.wireOp",EDGE,"E72.1");var subQ16=sQuery(id+"F12.wireOp",EDGE,"E74.1");var subQ18=sQuery(id+"F12.wireOp",EDGE,"E74.8");Q0=qUnion([makeQuery(id+"F12.imprint","IMPRINT",FACE,{"disambiguationData":[TD([[makeQuery(id+"F12.imprint","IMPRINT",EDGE,{"derivedFrom":subQ7}),1.0]])]}),makeQuery(id+"F12.imprint","IMPRINT",FACE,{"disambiguationData":[TD([[makeQuery(id+"F12.imprint","IMPRINT",EDGE,{"derivedFrom":subQ14}),1.0]])]}),makeQuery(id+"F12.imprint","IMPRINT",FACE,{"disambiguationData":[TD([[makeQuery(id+"F12.imprint","IMPRINT",EDGE,{"derivedFrom":subQ16}),1.0]])]}),makeQuery(id+"F12.imprint","IMPRINT",FACE,{"disambiguationData":[TD([[makeQuery(id+"F12.imprint","IMPRINT",EDGE,{"derivedFrom":subQ18}),-1.0]])]})]);}
            var Q1;
            Q1=makeQuery(id+"F5.boolean.opBoolean","SPLIT",FACE,{"disambiguationData":[TD([makeQuery(id+"F5.opExtrude","SWEPT_FACE",FACE,{"disambiguationData":[OSD([sQuery(id+"F4.wireOp",EDGE,"E41")])]})])],"derivedFrom":makeQuery(id+"F3.boolean.opBoolean","COPY",FACE,{"derivedFrom":makeQuery(id+"F3.opExtrude","CAP_FACE",FACE,{"disambiguationData":[OSD([sQuery(id+"F0.wireOp",EDGE,"E25.0"),sQuery(id+"F0.wireOp",EDGE,"E25.1"),sQuery(id+"F0.wireOp",EDGE,"E25.2"),sQuery(id+"F0.wireOp",EDGE,"E25.3"),sQuery(id+"F0.wireOp",EDGE,"E25.4"),sQuery(id+"F0.wireOp",EDGE,"E25.5"),sQuery(id+"F0.wireOp",EDGE,"E25.6"),sQuery(id+"F0.wireOp",EDGE,"E25.7")])],"isStart":false})})});
            extrude(context, id + "F13", {"entities" : qUnion([Q0]), "operationType" : NewBodyOperationType.REMOVE, "endBound" : BoundingType.UP_TO_SURFACE, "endBoundEntityFace" : qUnion([Q1]), "depth" : 25 * mm});
        }
        {
            var Q0;
            Q0=makeQuery(id+"F3.boolean.opBoolean","COPY",EDGE,{"derivedFrom":makeQuery(id+"F3.opExtrude","CAP_EDGE",EDGE,{"disambiguationData":[OSD([sQuery(id+"F0.wireOp",EDGE,"E25.6")])],"isStart":false})});
            var Q1;
            Q1=makeQuery(id+"F8.boolean.opBoolean","INTERSECT",EDGE,{"derivedFrom":[makeQuery(id+"F5.opExtrude","SWEPT_FACE",FACE,{"disambiguationData":[OSD([sQuery(id+"F4.wireOp",EDGE,"E30")])]}),makeQuery(id+"F8.opExtrude","CAP_FACE",FACE,{"disambiguationData":[OSD([sQuery(id+"F7.wireOp",EDGE,"E67")])],"isStart":false})]});
            var Q2;
            Q2=makeQuery(id+"F8.boolean.opBoolean","INTERSECT",EDGE,{"disambiguationData":[OD(1.0)],"derivedFrom":[makeQuery(id+"F5.opExtrude","SWEPT_FACE",FACE,{"disambiguationData":[OSD([sQuery(id+"F4.wireOp",EDGE,"E30")])]}),makeQuery(id+"F8.opExtrude","SWEPT_FACE",FACE,{"disambiguationData":[OSD([sQuery(id+"F7.wireOp",EDGE,"E67")])]})]});
            var Q3;
            {var subQ0=sQuery(id+"F4.wireOp",EDGE,"E30");Q3=makeQuery(id+"F8.boolean.opBoolean","SPLIT",EDGE,{"disambiguationData":[TD([makeQuery(id+"F5.opExtrude","SWEPT_FACE",FACE,{"disambiguationData":[OSD([sQuery(id+"F4.wireOp",EDGE,"E35.filletArc")])]})])],"derivedFrom":makeQuery(id+"F5.opExtrude","CAP_EDGE",EDGE,{"disambiguationData":[OSD([subQ0])],"isStart":false})});}
            var Q4;
            {var subQ0=sQuery(id+"F0.wireOp",EDGE,"E25.7");var subQ1=sQuery(id+"F0.wireOp",EDGE,"E25.1");var subQ2=sQuery(id+"F0.wireOp",EDGE,"E25.6");var subQ3=sQuery(id+"F0.wireOp",EDGE,"E25.5");var subQ4=sQuery(id+"F0.wireOp",EDGE,"E25.4");var subQ5=sQuery(id+"F0.wireOp",EDGE,"E25.0");var subQ6=sQuery(id+"F0.wireOp",EDGE,"E25.2");var subQ7=sQuery(id+"F0.wireOp",EDGE,"E25.3");Q4=makeQuery(id+"F8.boolean.opBoolean","INTERSECT",EDGE,{"derivedFrom":[makeQuery(id+"F5.boolean.opBoolean","SPLIT",FACE,{"disambiguationData":[TD([makeQuery(id+"F2.opExtrude","SWEPT_FACE",FACE,{"disambiguationData":[OSD([subQ5])]})])],"derivedFrom":makeQuery(id+"F3.boolean.opBoolean","COPY",FACE,{"derivedFrom":makeQuery(id+"F3.opExtrude","CAP_FACE",FACE,{"disambiguationData":[OSD([subQ5,subQ1,subQ6,subQ7,subQ4,subQ3,subQ2,subQ0])],"isStart":false})})}),makeQuery(id+"F8.opExtrude","SWEPT_FACE",FACE,{"disambiguationData":[OSD([sQuery(id+"F7.wireOp",EDGE,"E67")])]})]});}
            var Q5;
            Q5=makeQuery(id+"F8.boolean.opBoolean","INTERSECT",EDGE,{"disambiguationData":[OD(0.0)],"derivedFrom":[makeQuery(id+"F5.opExtrude","SWEPT_FACE",FACE,{"disambiguationData":[OSD([sQuery(id+"F4.wireOp",EDGE,"E30")])]}),makeQuery(id+"F8.opExtrude","SWEPT_FACE",FACE,{"disambiguationData":[OSD([sQuery(id+"F7.wireOp",EDGE,"E67")])]})]});
            fillet(context, id + "F14", {"entities" : qUnion([Q0, Q1, Q2, Q3, Q4, Q5]), "radius" : 3 * mm, "tangentPropagation" : true, "allowEdgeOverflow" : false});
        }
        {
            var Q0;
            Q0=makeQuery(id+"F1.opExtrude","CAP_EDGE",EDGE,{"disambiguationData":[OSD([sQuery(id+"F0.wireOp",EDGE,"E1.bottom")])],"isStart":false});
            fillet(context, id + "F15", {"entities" : qUnion([Q0]), "radius" : 2 * mm, "tangentPropagation" : true, "allowEdgeOverflow" : false});
        }
        {
            var Q0;
            {var subQ0=sQuery(id+"F0.wireOp",EDGE,"E21.filletArc");var subQ1=sQuery(id+"F0.wireOp",EDGE,"E7");var subQ2=sQuery(id+"F0.wireOp",EDGE,"E6");var subQ3=sQuery(id+"F0.wireOp",EDGE,"E5");var subQ4=sQuery(id+"F0.wireOp",EDGE,"E4");var subQ5=sQuery(id+"F0.wireOp",EDGE,"E22.filletArc");var subQ6=sQuery(id+"F0.wireOp",EDGE,"E1.bottom");var subQ7=sQuery(id+"F0.wireOp",EDGE,"E1.right");var subQ8=sQuery(id+"F0.wireOp",EDGE,"E1.top");var subQ9=sQuery(id+"F0.wireOp",EDGE,"E1.left");var subQ10=sQuery(id+"F0.wireOp",EDGE,"E23.filletArc");var subQ11=sQuery(id+"F0.wireOp",EDGE,"E24.filletArc");Q0=makeQuery(id+"F2.boolean.opBoolean","SPLIT",FACE,{"disambiguationData":[TD([makeQuery(id+"F1.opExtrude","SWEPT_FACE",FACE,{"disambiguationData":[OSD([subQ6])]})])],"derivedFrom":makeQuery(id+"F1.opExtrude","CAP_FACE",FACE,{"disambiguationData":[OSD([subQ6,subQ8,subQ9,subQ7,subQ4,subQ3,subQ2,subQ1,subQ0,subQ5,subQ10,subQ11])],"isStart":true})});}
            var sketch = newSketch(context, id + "F16", { "sketchPlane" : qUnion([Q0])});
            skLineSegment(sketch, "E79.0.0", {"start": v(70, 90) * mm, "end": v(-70, 90) * mm});
            skArc(sketch, "E79.0.1", {"start": v(-70, 90) * mm, "mid": v(-77.07, 87.07) * mm, "end": v(-80, 80) * mm});
            skLineSegment(sketch, "E79.0.2", {"start": v(-80, 80) * mm, "end": v(-80, -80) * mm});
            skArc(sketch, "E79.0.3", {"start": v(-80, -80) * mm, "mid": v(-77.07, -87.07) * mm, "end": v(-70, -90) * mm});
            skLineSegment(sketch, "E79.0.4", {"start": v(-70, -90) * mm, "end": v(70, -90) * mm});
            skArc(sketch, "E79.0.5", {"start": v(70, -90) * mm, "mid": v(77.07, -87.07) * mm, "end": v(80, -80) * mm});
            skLineSegment(sketch, "E79.0.6", {"start": v(80, -80) * mm, "end": v(80, 80) * mm});
            skArc(sketch, "E79.0.7", {"start": v(80, 80) * mm, "mid": v(77.07, 87.07) * mm, "end": v(70, 90) * mm});
            skArc(sketch, "E80.0", {"start": v(56.15, 48.18) * mm, "mid": v(0, 67.5) * mm, "end": v(-56.15, 48.18) * mm});
            skArc(sketch, "E81.0", {"start": v(-56.15, 48.18) * mm, "mid": v(-58.99, 44.68) * mm, "end": v(-60, 40.3) * mm});
            skLineSegment(sketch, "E82.0", {"start": v(-60, 40.3) * mm, "end": v(-60, -40.3) * mm});
            skArc(sketch, "E83.0", {"start": v(-60, -40.3) * mm, "mid": v(-58.99, -44.68) * mm, "end": v(-56.15, -48.18) * mm});
            skArc(sketch, "E84.0", {"start": v(-56.15, -48.18) * mm, "mid": v(0, -67.5) * mm, "end": v(56.15, -48.18) * mm});
            skArc(sketch, "E85.0", {"start": v(56.15, -48.18) * mm, "mid": v(58.99, -44.68) * mm, "end": v(60, -40.3) * mm});
            skLineSegment(sketch, "E86.0", {"start": v(60, 40.3) * mm, "end": v(60, -40.3) * mm});
            skArc(sketch, "E87.0", {"start": v(60, 40.3) * mm, "mid": v(58.99, 44.68) * mm, "end": v(56.15, 48.18) * mm});
            skLineSegment(sketch, "E88", {"start": v(0, 90) * mm, "end": v(0, 120) * mm, "construction": true});
            skCircle(sketch, "E89", {"center": v(0, 120) * mm, "radius": 6 * mm});
            skLineSegment(sketch, "E90", {"start": v(-33, 90) * mm, "end": v(-15, 108) * mm});
            skLineSegment(sketch, "E91", {"start": v(-15, 108) * mm, "end": v(-15, 120) * mm});
            skArc(sketch, "E92", {"start": v(15, 120) * mm, "mid": v(0, 135) * mm, "end": v(-15, 120) * mm});
            skLineSegment(sketch, "E93", {"start": v(15, 120) * mm, "end": v(15, 108) * mm});
            skLineSegment(sketch, "E94", {"start": v(15, 108) * mm, "end": v(33, 90) * mm});
            skLineSegment(sketch, "E95", {"start": v(-80, 0) * mm, "end": v(80, 0) * mm, "construction": true});
            skCircle(sketch, "E96.MirrorC", {"center": v(0, -120) * mm, "radius": 6 * mm});
            skLineSegment(sketch, "E97.MirrorCS", {"start": v(-33, -90) * mm, "end": v(-15, -108) * mm});
            skLineSegment(sketch, "E98.MirrorCS", {"start": v(-15, -108) * mm, "end": v(-15, -120) * mm});
            skLineSegment(sketch, "E99.MirrorCS", {"start": v(15, -120) * mm, "end": v(15, -108) * mm});
            skLineSegment(sketch, "E100.MirrorCS", {"start": v(15, -108) * mm, "end": v(33, -90) * mm});
            skArc(sketch, "E101.MirrorCS", {"start": v(15, -120) * mm, "mid": v(0, -135) * mm, "end": v(-15, -120) * mm});
            skSolve(sketch);
        }
        {
            var Q0;
            Q0=makeQuery(id+"F16.imprint","IMPRINT",FACE,{"disambiguationData":[TD([[makeQuery(id+"F16.imprint","IMPRINT",EDGE,{"derivedFrom":sQuery(id+"F16.wireOp",EDGE,"E96.MirrorC")}),1.0]])]});
            var Q1;
            {var subQ1=sQuery(id+"F16.wireOp",EDGE,"E79.0.1");Q1=makeQuery(id+"F16.imprint","IMPRINT",FACE,{"disambiguationData":[TD([[makeQuery(id+"F16.imprint","IMPRINT",EDGE,{"derivedFrom":subQ1}),1.0]])]});}
            var Q2;
            Q2=makeQuery(id+"F16.imprint","IMPRINT",FACE,{"disambiguationData":[TD([[makeQuery(id+"F16.imprint","IMPRINT",EDGE,{"derivedFrom":sQuery(id+"F16.wireOp",EDGE,"E89")}),-1.0]])]});
            var Q3;
            Q3=makeQuery(id+"F2.opExtrude","CAP_FACE",FACE,{"disambiguationData":[OSD([sQuery(id+"F0.wireOp",EDGE,"E12"),sQuery(id+"F0.wireOp",EDGE,"E13"),sQuery(id+"F0.wireOp",EDGE,"E14"),sQuery(id+"F0.wireOp",EDGE,"E15"),sQuery(id+"F0.wireOp",EDGE,"E17.filletArc"),sQuery(id+"F0.wireOp",EDGE,"E18.filletArc"),sQuery(id+"F0.wireOp",EDGE,"E19.filletArc"),sQuery(id+"F0.wireOp",EDGE,"E20.filletArc"),sQuery(id+"F0.wireOp",EDGE,"E25.0"),sQuery(id+"F0.wireOp",EDGE,"E25.1"),sQuery(id+"F0.wireOp",EDGE,"E25.2"),sQuery(id+"F0.wireOp",EDGE,"E25.3"),sQuery(id+"F0.wireOp",EDGE,"E25.4"),sQuery(id+"F0.wireOp",EDGE,"E25.5"),sQuery(id+"F0.wireOp",EDGE,"E25.6"),sQuery(id+"F0.wireOp",EDGE,"E25.7")])],"isStart":false});
            extrude(context, id + "F17", {"entities" : qUnion([Q0, Q1, Q2]), "endBound" : BoundingType.UP_TO_SURFACE, "depth" : 25 * mm, "endBoundEntityFace" : qUnion([Q3]), "offsetDistance" : 25 * mm});
        }
    });
